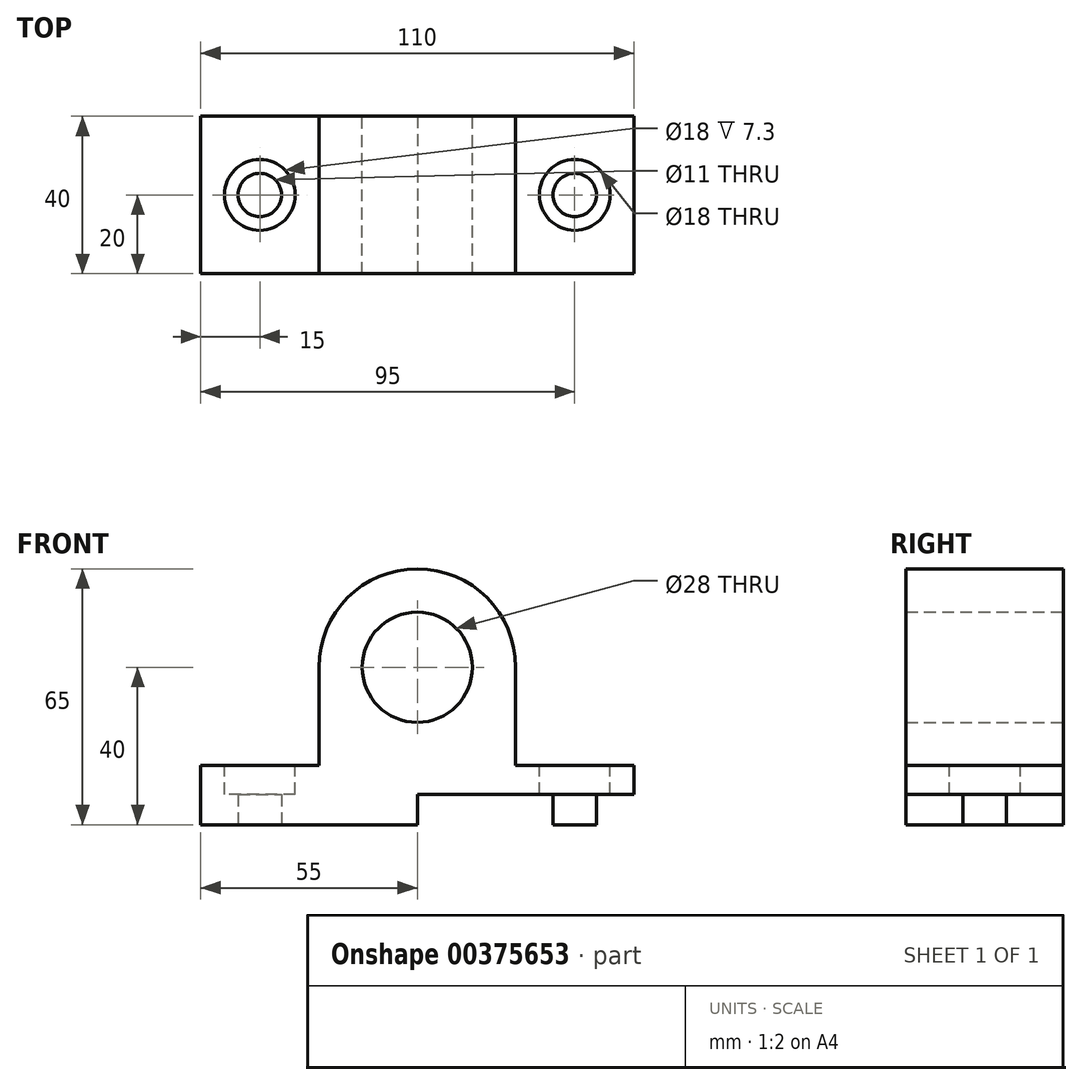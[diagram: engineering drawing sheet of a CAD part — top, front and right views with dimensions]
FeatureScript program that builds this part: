
annotation { "Feature Type Name" : "Feature", "Feature Type Description" : "" }
export const myFeature = defineFeature(function(context is Context, id is Id, definition is map)
    precondition{}
    {
        {
            var Q0;
            Q0=qCreatedBy(makeId("Front.planeOp"),FACE);
            var sketch = newSketch(context, id + "F0", { "sketchPlane" : qUnion([Q0])});
            skLineSegment(sketch, "E0", {"start": v(0, 0) * mm, "end": v(110, 0) * mm});
            skLineSegment(sketch, "E1", {"start": v(110, 0) * mm, "end": v(110, 15) * mm});
            skLineSegment(sketch, "E2", {"start": v(110, 15) * mm, "end": v(80, 15) * mm});
            skLineSegment(sketch, "E3", {"start": v(80, 15) * mm, "end": v(80, 40) * mm});
            skLineSegment(sketch, "E4", {"start": v(30, 40) * mm, "end": v(30, 15) * mm});
            skLineSegment(sketch, "E5", {"start": v(30, 15) * mm, "end": v(0, 15) * mm});
            skLineSegment(sketch, "E6", {"start": v(0, 15) * mm, "end": v(0, 0) * mm});
            skCircle(sketch, "E7", {"center": v(55, 40) * mm, "radius": 14 * mm});
            skArc(sketch, "E8", {"start": v(80, 40) * mm, "mid": v(55, 65) * mm, "end": v(30, 40) * mm});
            skLineSegment(sketch, "E9", {"start": v(55, 75.92) * mm, "end": v(55, -32.58) * mm});
            skSolve(sketch);
        }
        {
            var Q0;
            Q0=makeQuery(id+"F0.imprint","IMPRINT",FACE,{"disambiguationData":[TD([[makeQuery(id+"F0.imprint","IMPRINT",EDGE,{"derivedFrom":sQuery(id+"F0.wireOp",EDGE,"E0")}),1.0]])]});
            extrude(context, id + "F1", {"entities" : qUnion([Q0]), "depth" : 40 * mm});
        }
        {
            var Q0;
            Q0=makeQuery(id+"F1.opExtrude","SWEPT_FACE",FACE,{"disambiguationData":[OSD([sQuery(id+"F0.wireOp",EDGE,"E5")])]});
            var sketch = newSketch(context, id + "F2", { "sketchPlane" : qUnion([Q0])});
            skCircle(sketch, "E10", {"center": v(15, -20) * mm, "radius": 9 * mm});
            skSolve(sketch);
        }
        {
            var Q0;
            Q0=makeQuery(id+"F2.imprint","IMPRINT",FACE,{"disambiguationData":[TD([[makeQuery(id+"F2.imprint","IMPRINT",EDGE,{"derivedFrom":sQuery(id+"F2.wireOp",EDGE,"E10")}),1.0]])]});
            extrude(context, id + "F3", {"entities" : qUnion([Q0]), "operationType" : NewBodyOperationType.REMOVE, "oppositeDirection" : true, "depth" : 7.3 * mm});
        }
        {
            var Q0;
            Q0=makeQuery(id+"F1.opExtrude","SWEPT_FACE",FACE,{"disambiguationData":[OSD([sQuery(id+"F0.wireOp",EDGE,"E0")])]});
            var sketch = newSketch(context, id + "F4", { "sketchPlane" : qUnion([Q0])});
            skLineSegment(sketch, "E11", {"start": v(55, 0) * mm, "end": v(55, 64.3) * mm});
            skCircle(sketch, "E12", {"center": v(15, 20) * mm, "radius": 5.5 * mm});
            skCircle(sketch, "E13.MirrorC", {"center": v(95, 20) * mm, "radius": 5.5 * mm});
            skSolve(sketch);
        }
        {
            var Q0;
            Q0=makeQuery(id+"F4.imprint","IMPRINT",FACE,{"disambiguationData":[TD([[makeQuery(id+"F4.imprint","IMPRINT",EDGE,{"derivedFrom":sQuery(id+"F4.wireOp",EDGE,"E12")}),1.0]])]});
            var Q1;
            Q1=makeQuery(id+"F4.imprint","IMPRINT",FACE,{"disambiguationData":[TD([[makeQuery(id+"F4.imprint","IMPRINT",EDGE,{"derivedFrom":sQuery(id+"F4.wireOp",EDGE,"E13.MirrorC")}),-1.0]])]});
            extrude(context, id + "F5", {"entities" : qUnion([Q0, Q1]), "operationType" : NewBodyOperationType.REMOVE, "oppositeDirection" : true, "depth" : 7.7 * mm});
        }
        {
            var Q0;
            Q0=makeQuery(id+"F1.opExtrude","SWEPT_FACE",FACE,{"disambiguationData":[OSD([sQuery(id+"F0.wireOp",EDGE,"E2")])]});
            var sketch = newSketch(context, id + "F6", { "sketchPlane" : qUnion([Q0])});
            skCircle(sketch, "E14", {"center": v(95, -20) * mm, "radius": 9 * mm});
            skSolve(sketch);
        }
        {
            var Q0;
            Q0=makeQuery(id+"F6.imprint","IMPRINT",FACE,{"disambiguationData":[TD([[makeQuery(id+"F6.imprint","IMPRINT",EDGE,{"derivedFrom":sQuery(id+"F6.wireOp",EDGE,"E14")}),1.0]])]});
            extrude(context, id + "F7", {"entities" : qUnion([Q0]), "operationType" : NewBodyOperationType.REMOVE, "oppositeDirection" : true, "depth" : 7.3 * mm});
        }
    });
